# Revit family: 28_HEA
name_source: partatom
category: Structural Columns
units: mm (PartAtom-declared; Revit-internal decimal feet)

## family parameters
Always export as geometry = No
Beam cutback in plan = From bounding box
Cut with Voids When Loaded = No
Material for Model Behavior = Steel
Section Shape = Not Defined
Shared = No
Show family pre-cut in plan views = Yes

## types (5) — shared parameters

## per-type parameters (varying)
| type | A | W | bf | d | k | kr | tf | tw |
| HEA180 | 0 m² | 0.241832 | 180 mm  [stored 0.590551 ft] | 171 mm  [stored 0.561024 ft] | 21 mm  [stored 0.0688976 ft] | 11 mm | 10 mm  [stored 0.0328084 ft] | 6 mm  [stored 0.019685 ft] |
| HEA240 | 0.01 m² | 0.591341 | 240 mm  [stored 0.787402 ft] | 230 mm  [stored 0.754593 ft] | 33 mm  [stored 0.108268 ft] | 21 mm  [stored 0.0688976 ft] | 12 mm  [stored 0.0393701 ft] | 8 mm  [stored 0.0262467 ft] |
| HEA200 | 0.01 m² | 0.414821 | 200 mm  [stored 0.656168 ft] | 190 mm | 28 mm  [stored 0.0918635 ft] | 18 mm  [stored 0.0590551 ft] | 10 mm  [stored 0.0328084 ft] | 7 mm  [stored 0.0229659 ft] |
| HEA140 | 0 m² | 0.241832 | 140 mm  [stored 0.459318 ft] | 133 mm  [stored 0.436352 ft] | 21 mm  [stored 0.0688976 ft] | 12 mm  [stored 0.0393701 ft] | 9 mm  [stored 0.0295276 ft] | 6 mm  [stored 0.019685 ft] |
| HEA100 | 0 m² | 0.163477 | 100 mm  [stored 0.328084 ft] | 96 mm  [stored 0.314961 ft] | 20 mm  [stored 0.0656168 ft] | 12 mm  [stored 0.0393701 ft] | 8 mm  [stored 0.0262467 ft] | 5 mm  [stored 0.0164042 ft] |

note: [stored X ft] marks values corroborated as IEEE doubles in the binary element streams (Revit-internal decimal feet)

## geometry (parser evidence)
native form markers: Sweep x1
no freeform markers — native parametric forms only
